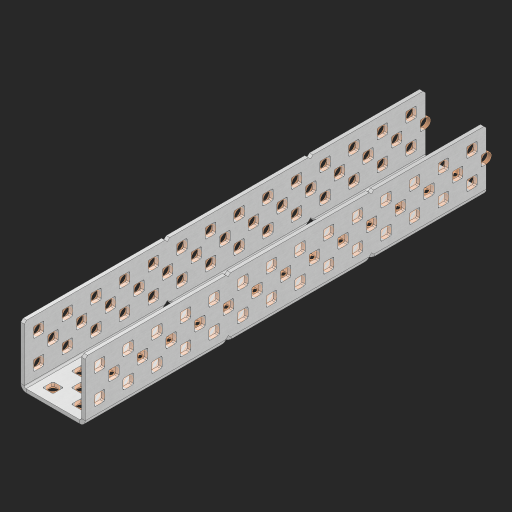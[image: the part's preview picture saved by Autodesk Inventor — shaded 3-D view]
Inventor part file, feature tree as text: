
AUTODESK INVENTOR PART (.ipt)
format: ipt  version: 2023 (Build 270158000, 158)  size: 1,740,288 bytes
history: native  units: in
note: dims shown in document units (in); Inventor stores cm internally (conversion verified against a paired STEP export)
features: other x174, extrude x166, sheet_metal_op x8, sketch x7, mirror x3, pattern_linear x2, chamfer x1
ambient origin geometry x8: Origin, YZ Plane, XZ Plane, XY Plane, X Axis, Y Axis, Z Axis, Center Point
bodies: Solid1 (feature_tree), Body (feature_tree)
feature tree (361):
  sheet_metal_op  "Flanges"
  sheet_metal_op  "Body Pattern"
  pattern_linear  "Center Pattern"  Spacing1=1.0in  [1 undecoded]
  other  "Arc Length"
  mirror  "Notch Mirror"
  pattern_linear  "Notch Pattern"  Spacing1=0.25in  [1 undecoded]
  other  "Diagonal Plane"
  mirror  "Flange 1"
  mirror  "Flange 2"
  chamfer  "End Chamfer"
  sketch  "Sketch1"  dims[d0=1.0in]
  other  "Plate1"
  sketch  "Sketch2"  dims[d1=7.0in]
  other  "Plate2"
  sheet_metal_op  "Bend1"
  sheet_metal_op  "Corner1"
  sketch  "Sketch8"  dims[d2=0.0625in]
  sketch  "Sketch9"  dims[d3=0.0625in]
  other  "Srf91"
  sheet_metal_op  "Body Pattern Sketch"
  other  "Srf92"
  sketch  "Sketch13"  dims[d4=0.0312in]
  sketch  "Sketch15"  dims[d5=0.125in]
  sketch  "Sketch16"  dims[d6=0.0625in d7=1.0in d8=90.0deg d9=0.0312in d10=0.25in d11=0.0625in d12=0.0625in d49=0.182in d50=0.02in d52=0.25in d53=0.0625in d54=0.0in d55=0.172in d56=1.0in d57=0.0in d60=5.5118in d62=0.5in d63=0.7874in d65=0.5in d85=0.1473in d86=0.1782in d88=0.04in d89=0.0625in d90=0.0in d91=0.04in d92=0.0491in d95=2.5in d96=0.04in d97=0.25in d98=45.0deg d99=0.25in d102=2.497in d106=0.182in d107=0.02in d108=0.5in d110=0.0625in d111=0.0in d112=0.172in d113=0.5in d114=0.0in d117=0.5in d118=0.5in d131=0.25in d132=0.25in]
  other  "Srf786"
  other  "Srf889"
  other  "Srf890"
  other  "Srf891"
  other  "Srf892"
  other  "Srf893"
  other  "Srf894"
  other  "Srf895"
  other  "Srf896"
  other  "Srf996"
  other  "Srf997"
  other  "Srf998"
  other  "Srf999"
  other  "Srf1000"
  other  "Srf1315"
  other  "Srf1316"
  other  "Srf1317"
  other  "Srf1325"
  other  "Srf1326"
  other  "Srf1327"
  other  "Srf1328"
  other  "Srf1329"
  other  "Srf1330"
  other  "Srf1331"
  other  "Srf1332"
  other  "Srf1338"
  other  "Srf1339"
  other  "Srf1340"
  other  "Srf1341"
  other  "Srf1342"
  other  "Srf1374"
  other  "Srf1375"
  other  "Srf1376"
  other  "Srf1384"
  other  "Srf1385"
  other  "Srf1386"
  other  "Srf1387"
  other  "Srf1388"
  other  "Srf1389"
  other  "Srf1390"
  other  "Srf1391"
  other  "Srf1397"
  other  "Srf1398"
  other  "Srf1399"
  other  "Srf1400"
  other  "Srf1401"
  other  "Srf1433"
  other  "Srf1434"
  other  "Srf1473"
  other  "Srf1474"
  other  "Srf1475"
  other  "Srf1476"
  other  "Srf1477"
  other  "Srf1478"
  other  "Srf1479"
  other  "Srf1480"
  other  "Srf1481"
  other  "Srf1482"
  other  "Srf1483"
  other  "Srf1484"
  other  "Srf1485"
  other  "Srf1486"
  other  "Srf1500"
  other  "Srf1501"
  other  "Srf1502"
  other  "Srf1503"
  other  "Srf1504"
  other  "Srf1505"
  other  "Srf1506"
  other  "Srf1507"
  other  "Srf1508"
  other  "Srf1509"
  other  "Srf1510"
  other  "Srf1511"
  other  "Srf1512"
  other  "Srf1513"
  other  "Srf1514"
  other  "Srf1515"
  other  "Srf1516"
  other  "Srf1517"
  other  "Srf1518"
  other  "Srf1519"
  other  "Srf1520"
  other  "Srf1521"
  other  "Srf1522"
  other  "Srf1523"
  other  "Srf1524"
  other  "Srf1525"
  other  "Srf1538"
  other  "Srf1539"
  other  "Srf1540"
  other  "Srf1541"
  other  "Srf1542"
  other  "Srf1543"
  other  "Srf1544"
  other  "Srf1545"
  other  "Srf1546"
  other  "Srf1547"
  other  "Srf1548"
  other  "Srf1549"
  other  "Srf1550"
  other  "Srf1551"
  other  "Srf1552"
  other  "Srf1553"
  other  "Srf1554"
  other  "Srf1555"
  other  "Srf1556"
  other  "Srf1557"
  other  "Srf1558"
  other  "Srf1559"
  other  "Srf1560"
  other  "Srf1561"
  other  "Srf1562"
  other  "Srf1563"
  other  "Srf1576"
  other  "Srf1577"
  other  "Srf1578"
  other  "Srf1579"
  other  "Srf1580"
  other  "Srf1581"
  other  "Srf1582"
  other  "Srf1583"
  other  "Srf1584"
  other  "Srf1585"
  other  "Srf1586"
  other  "Srf1587"
  other  "Srf1588"
  other  "Srf1589"
  other  "Srf1590"
  other  "Srf1591"
  other  "Srf1592"
  other  "Srf1593"
  other  "Srf1594"
  other  "Srf1595"
  other  "Srf1596"
  other  "Srf1597"
  other  "Srf1598"
  other  "Srf1599"
  other  "Srf1600"
  other  "Srf1601"
  other  "Srf1614"
  other  "Srf1615"
  other  "Srf1616"
  other  "Srf1617"
  other  "Srf1618"
  other  "Srf1619"
  other  "Srf1620"
  other  "Srf1621"
  other  "Srf1622"
  other  "Srf1623"
  other  "Srf1624"
  other  "Srf1625"
  other  "Srf1626"
  other  "Srf1627"
  other  "Srf1628"
  other  "Srf1629"
  other  "Srf1630"
  other  "Srf1631"
  other  "Srf1632"
  other  "Srf1633"
  other  "Srf1634"
  other  "Srf1635"
  other  "Srf1636"
  other  "Srf1637"
  other  "Srf1638"
  other  "Srf1639"
  sheet_metal_op  "Body Stamp"
  sheet_metal_op  "Body Circle"
  other  "Center Stamp"
  other  "Center Circle"
  sheet_metal_op  "Notch"
  extrude  "ExtrusionSrf92"  Depth=0.0625in
  extrude  "ExtrusionSrf889"  Depth=0.0625in
  extrude  "ExtrusionSrf890"  Depth=0.182in
  extrude  "ExtrusionSrf891"  Depth=0.02in
  extrude  "ExtrusionSrf892"  Depth=0.25in
  extrude  "ExtrusionSrf893"  Depth=0.0625in
  extrude  "ExtrusionSrf894"  TaperAngle=0.0deg  [1 undecoded]
  extrude  "ExtrusionSrf895"  Depth=0.25in
  extrude  "ExtrusionSrf896"  Depth=1.0in TaperAngle=0.0deg
  extrude  "ExtrusionSrf996"  Depth=0.25in
  extrude  "ExtrusionSrf997"  Depth=0.5in
  extrude  "ExtrusionSrf998"  Depth=0.25in
  extrude  "ExtrusionSrf999"  Depth=0.25in
  extrude  "ExtrusionSrf1000"  Depth=0.25in
  extrude  "ExtrusionSrf1315"  Depth=0.0625in
  extrude  "ExtrusionSrf1316"  TaperAngle=0.0deg  [1 undecoded]
  extrude  "ExtrusionSrf1355"  Depth=0.25in
  extrude  "ExtrusionSrf1356"  Depth=0.25in
  extrude  "ExtrusionSrf1357"  Depth=2.5in
  extrude  "ExtrusionSrf1358"  Depth=0.25in TaperAngle=45.0deg
  extrude  "ExtrusionSrf1359"  Depth=0.25in
  extrude  "ExtrusionSrf1360"  Depth=0.25in
  extrude  "ExtrusionSrf1361"  Depth=0.182in
  extrude  "ExtrusionSrf1362"  Depth=0.02in
  extrude  "ExtrusionSrf1363"  Depth=0.5in
  extrude  "ExtrusionSrf1364"  Depth=0.0625in
  extrude  "ExtrusionSrf1365"  TaperAngle=0.0deg  [1 undecoded]
  extrude  "ExtrusionSrf1366"  Depth=0.25in
  extrude  "ExtrusionSrf1367"  Depth=0.5in TaperAngle=0.0deg
  extrude  "ExtrusionSrf1368"  Depth=0.5in
  extrude  "ExtrusionSrf1374"  Depth=0.5in
  extrude  "ExtrusionSrf1375"  Depth=0.25in
  extrude  "ExtrusionSrf1414"  Depth=0.25in
  extrude  "ExtrusionSrf1415"  [1 undecoded]
  extrude  "ExtrusionSrf1416"  [1 undecoded]
  extrude  "ExtrusionSrf1417"  [1 undecoded]
  extrude  "ExtrusionSrf1418"  [1 undecoded]
  extrude  "ExtrusionSrf1419"  [1 undecoded]
  extrude  "ExtrusionSrf1420"  [1 undecoded]
  extrude  "ExtrusionSrf1421"  [1 undecoded]
  extrude  "ExtrusionSrf1422"  [1 undecoded]
  extrude  "ExtrusionSrf1423"  [1 undecoded]
  extrude  "ExtrusionSrf1424"  [1 undecoded]
  extrude  "ExtrusionSrf1425"  [1 undecoded]
  extrude  "ExtrusionSrf1426"  [1 undecoded]
  extrude  "ExtrusionSrf1427"  [1 undecoded]
  extrude  "ExtrusionSrf1433"  [1 undecoded]
  extrude  "ExtrusionSrf1434"  [1 undecoded]
  extrude  "ExtrusionSrf1473"  [1 undecoded]
  extrude  "ExtrusionSrf1474"  [1 undecoded]
  extrude  "ExtrusionSrf1475"  [1 undecoded]
  extrude  "ExtrusionSrf1476"  [1 undecoded]
  extrude  "ExtrusionSrf1477"  [1 undecoded]
  extrude  "ExtrusionSrf1478"  [1 undecoded]
  extrude  "ExtrusionSrf1479"  [1 undecoded]
  extrude  "ExtrusionSrf1480"  [1 undecoded]
  extrude  "ExtrusionSrf1481"  [1 undecoded]
  extrude  "ExtrusionSrf1482"  [1 undecoded]
  extrude  "ExtrusionSrf1483"  [1 undecoded]
  extrude  "ExtrusionSrf1484"  [1 undecoded]
  extrude  "ExtrusionSrf1485"  [1 undecoded]
  extrude  "ExtrusionSrf1486"  [1 undecoded]
  extrude  "ExtrusionSrf1500"  [1 undecoded]
  extrude  "ExtrusionSrf1501"  [1 undecoded]
  extrude  "ExtrusionSrf1502"  [1 undecoded]
  extrude  "ExtrusionSrf1503"  [1 undecoded]
  extrude  "ExtrusionSrf1504"  [1 undecoded]
  extrude  "ExtrusionSrf1505"  [1 undecoded]
  extrude  "ExtrusionSrf1506"  [1 undecoded]
  extrude  "ExtrusionSrf1507"  [1 undecoded]
  extrude  "ExtrusionSrf1508"  [1 undecoded]
  extrude  "ExtrusionSrf1509"  [1 undecoded]
  extrude  "ExtrusionSrf1510"  [1 undecoded]
  extrude  "ExtrusionSrf1511"  [1 undecoded]
  extrude  "ExtrusionSrf1512"  [1 undecoded]
  extrude  "ExtrusionSrf1513"  [1 undecoded]
  extrude  "ExtrusionSrf1514"  [1 undecoded]
  extrude  "ExtrusionSrf1515"  [1 undecoded]
  extrude  "ExtrusionSrf1516"  [1 undecoded]
  extrude  "ExtrusionSrf1517"  [1 undecoded]
  extrude  "ExtrusionSrf1518"  [1 undecoded]
  extrude  "ExtrusionSrf1519"  [1 undecoded]
  extrude  "ExtrusionSrf1520"  [1 undecoded]
  extrude  "ExtrusionSrf1521"  [1 undecoded]
  extrude  "ExtrusionSrf1522"  [1 undecoded]
  extrude  "ExtrusionSrf1523"  [1 undecoded]
  extrude  "ExtrusionSrf1524"  [1 undecoded]
  extrude  "ExtrusionSrf1525"  [1 undecoded]
  extrude  "ExtrusionSrf1538"  [1 undecoded]
  extrude  "ExtrusionSrf1539"  [1 undecoded]
  extrude  "ExtrusionSrf1540"  [1 undecoded]
  extrude  "ExtrusionSrf1541"  [1 undecoded]
  extrude  "ExtrusionSrf1542"  [1 undecoded]
  extrude  "ExtrusionSrf1543"  [1 undecoded]
  extrude  "ExtrusionSrf1544"  [1 undecoded]
  extrude  "ExtrusionSrf1545"  [1 undecoded]
  extrude  "ExtrusionSrf1546"  [1 undecoded]
  extrude  "ExtrusionSrf1547"  [1 undecoded]
  extrude  "ExtrusionSrf1548"  [1 undecoded]
  extrude  "ExtrusionSrf1549"  [1 undecoded]
  extrude  "ExtrusionSrf1550"  [1 undecoded]
  extrude  "ExtrusionSrf1551"  [1 undecoded]
  extrude  "ExtrusionSrf1552"  [1 undecoded]
  extrude  "ExtrusionSrf1553"  [1 undecoded]
  extrude  "ExtrusionSrf1554"  [1 undecoded]
  extrude  "ExtrusionSrf1555"  [1 undecoded]
  extrude  "ExtrusionSrf1556"  [1 undecoded]
  extrude  "ExtrusionSrf1557"  [1 undecoded]
  extrude  "ExtrusionSrf1558"  [1 undecoded]
  extrude  "ExtrusionSrf1559"  [1 undecoded]
  extrude  "ExtrusionSrf1560"  [1 undecoded]
  extrude  "ExtrusionSrf1561"  [1 undecoded]
  extrude  "ExtrusionSrf1562"  [1 undecoded]
  extrude  "ExtrusionSrf1563"  [1 undecoded]
  extrude  "ExtrusionSrf1576"  [1 undecoded]
  extrude  "ExtrusionSrf1577"  [1 undecoded]
  extrude  "ExtrusionSrf1578"  [1 undecoded]
  extrude  "ExtrusionSrf1579"  [1 undecoded]
  extrude  "ExtrusionSrf1580"  [1 undecoded]
  extrude  "ExtrusionSrf1581"  [1 undecoded]
  extrude  "ExtrusionSrf1582"  [1 undecoded]
  extrude  "ExtrusionSrf1583"  [1 undecoded]
  extrude  "ExtrusionSrf1584"  [1 undecoded]
  extrude  "ExtrusionSrf1585"  [1 undecoded]
  extrude  "ExtrusionSrf1586"  [1 undecoded]
  extrude  "ExtrusionSrf1587"  [1 undecoded]
  extrude  "ExtrusionSrf1588"  [1 undecoded]
  extrude  "ExtrusionSrf1589"  [1 undecoded]
  extrude  "ExtrusionSrf1590"  [1 undecoded]
  extrude  "ExtrusionSrf1591"  [1 undecoded]
  extrude  "ExtrusionSrf1592"  [1 undecoded]
  extrude  "ExtrusionSrf1593"  [1 undecoded]
  extrude  "ExtrusionSrf1594"  [1 undecoded]
  extrude  "ExtrusionSrf1595"  [1 undecoded]
  extrude  "ExtrusionSrf1596"  [1 undecoded]
  extrude  "ExtrusionSrf1597"  [1 undecoded]
  extrude  "ExtrusionSrf1598"  [1 undecoded]
  extrude  "ExtrusionSrf1599"  [1 undecoded]
  extrude  "ExtrusionSrf1600"  [1 undecoded]
  extrude  "ExtrusionSrf1601"  [1 undecoded]
  extrude  "ExtrusionSrf1614"  [1 undecoded]
  extrude  "ExtrusionSrf1615"  [1 undecoded]
  extrude  "ExtrusionSrf1616"  [1 undecoded]
  extrude  "ExtrusionSrf1617"  [1 undecoded]
  extrude  "ExtrusionSrf1618"  [1 undecoded]
  extrude  "ExtrusionSrf1619"  [1 undecoded]
  extrude  "ExtrusionSrf1620"  [1 undecoded]
  extrude  "ExtrusionSrf1621"  [1 undecoded]
  extrude  "ExtrusionSrf1622"  [1 undecoded]
  extrude  "ExtrusionSrf1623"  [1 undecoded]
  extrude  "ExtrusionSrf1624"  [1 undecoded]
  extrude  "ExtrusionSrf1625"  [1 undecoded]
  extrude  "ExtrusionSrf1626"  [1 undecoded]
  extrude  "ExtrusionSrf1627"  [1 undecoded]
  extrude  "ExtrusionSrf1628"  [1 undecoded]
  extrude  "ExtrusionSrf1629"  [1 undecoded]
  extrude  "ExtrusionSrf1630"  [1 undecoded]
  extrude  "ExtrusionSrf1631"  [1 undecoded]
  extrude  "ExtrusionSrf1632"  [1 undecoded]
  extrude  "ExtrusionSrf1633"  [1 undecoded]
  extrude  "ExtrusionSrf1634"  [1 undecoded]
  extrude  "ExtrusionSrf1635"  [1 undecoded]
  extrude  "ExtrusionSrf1636"  [1 undecoded]
  extrude  "ExtrusionSrf1637"  [1 undecoded]
  extrude  "ExtrusionSrf1638"  [1 undecoded]
  extrude  "ExtrusionSrf1639"  [1 undecoded]
note: 138 required parameter values undecoded (feature->parameter linkage not recoverable at this tier; creation-order binding heuristic only, values carry confidence <= 0.55)
